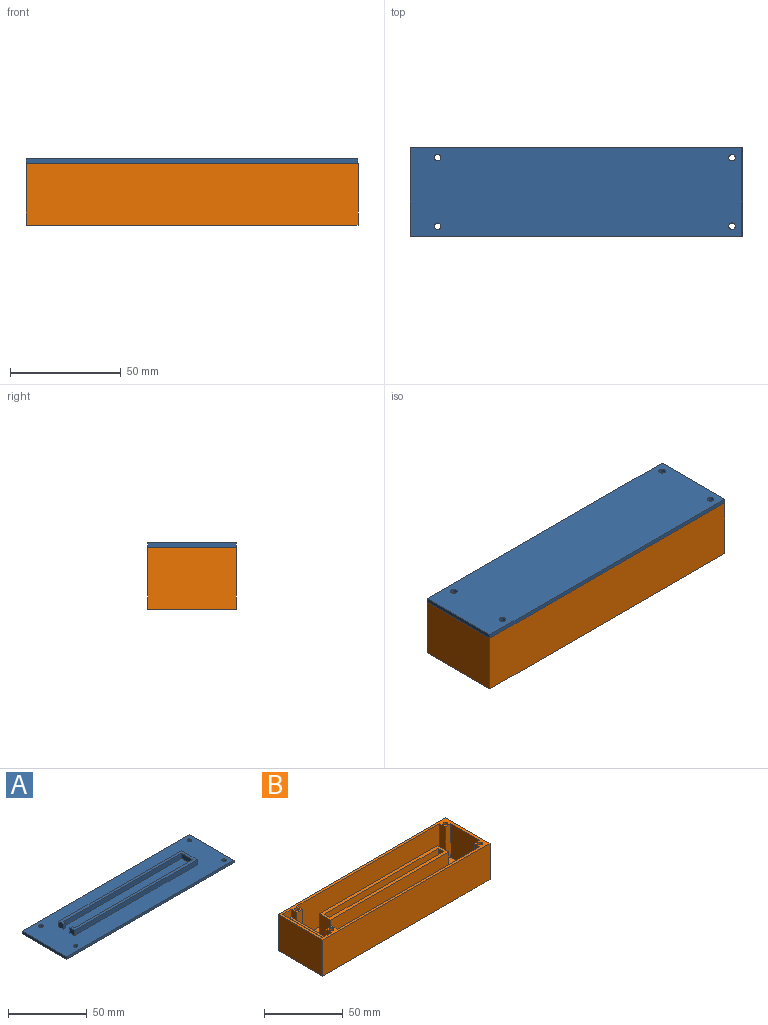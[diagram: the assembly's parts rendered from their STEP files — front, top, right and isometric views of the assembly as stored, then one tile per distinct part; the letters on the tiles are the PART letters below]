
ASSEMBLY  parts=2 mates=1
PART A: 23 faces, bbox 150x40x6 mm
  f0: plane 150x2mm, normal (0,-1,0), area 300mm2, adj f1,f6,f8,f9
  f1: plane 40x2mm, normal (1,0,0), area 80mm2, adj f0,f2,f8,f9
  f2: plane 150x2mm, normal (0,1,0), area 300mm2, adj f1,f6,f8,f9
  f3: cylinder r=1.5mm len=3mm, axis (0,0,-1), area 18.8mm2, adj f8,f9
  f4: cylinder r=1.5mm len=3mm, axis (0,0,-1), area 18.8mm2, adj f8,f9
  f5: cylinder r=1.5mm len=3mm, axis (0,0,-1), area 18.8mm2, adj f8,f9
  f6: plane 40x2mm, normal (-1,0,0), area 80mm2, adj f0,f2,f8,f9
  f7: cylinder r=1.5mm len=3mm, axis (0,0,-1), area 18.8mm2, adj f8,f9
  f8: plane 150x40mm, normal (0,0,1), area 5503.7mm2, adj f0,f1,f2,f3,f4,f5,f6,f7
  f9: plane 150x40mm, normal (0,0,-1), area 5971.7mm2, adj f0,f1,f2,f3,f4,f5,f6,f7
  f10: plane 4x2mm, normal (1,0,0), area 8mm2, adj f8,f11,f21,f22
  f11: plane 4x2mm, normal (0,1,0), area 8mm2, adj f8,f10,f12,f22
  f12: plane 4x4mm, normal (-1,0,0), area 16mm2, adj f8,f11,f13,f22
  f13: plane 110x4mm, normal (0,-1,0), area 440mm2, adj f8,f12,f14,f22
  f14: plane 14x4mm, normal (1,0,0), area 56mm2, adj f8,f13,f15,f22
  f15: plane 110x4mm, normal (0,1,0), area 440mm2, adj f8,f14,f16,f22
  f16: plane 4x4mm, normal (-1,0,0), area 16mm2, adj f8,f15,f17,f22
  f17: plane 4x2mm, normal (0,-1,0), area 8mm2, adj f8,f16,f18,f22
  f18: plane 4x2mm, normal (1,0,0), area 8mm2, adj f8,f17,f19,f22
  f19: plane 106x4mm, normal (0,-1,0), area 424mm2, adj f8,f18,f20,f22
  f20: plane 10x4mm, normal (-1,0,0), area 40mm2, adj f8,f19,f21,f22
  f21: plane 106x4mm, normal (0,1,0), area 424mm2, adj f8,f10,f20,f22
  f22: plane 110x14mm, normal (0,0,1), area 468mm2, adj f10,f11,f12,f13,f14,f15,f16,f17
PART B: 43 faces, bbox 150x40x28 mm
  f0: plane 8x6mm, normal (0,-1,0), area 48mm2, adj f3,f13,f39,f42
  f1: plane 150x28mm, normal (0,1,0), area 4140mm2, adj f5,f6,f12,f13,f28,f39,f41,f42
  f2: plane 8x8mm, normal (0,-1,0), area 60mm2, adj f13,f14,f28,f39,f40,f41
  f3: plane 36x6mm, normal (0,0,1), area 216mm2, adj f0,f13,f27,f39
  f4: plane 150x28mm, normal (0,-1,0), area 4200mm2, adj f5,f6,f12,f28
  f5: plane 40x28mm, normal (1,0,0), area 1120mm2, adj f1,f4,f12,f28
  f6: plane 40x28mm, normal (-1,0,0), area 1120mm2, adj f1,f4,f12,f28
  f7: cylinder r=1.5mm len=28mm, axis (0,0,-1), area 263.9mm2, adj f12,f28
  f8: cylinder r=1.5mm len=28mm, axis (0,0,-1), area 263.9mm2, adj f12,f28
  f9: cylinder r=1.5mm len=28mm, axis (0,0,-1), area 263.9mm2, adj f12,f28
  f10: cylinder r=1.5mm len=28mm, axis (0,0,-1), area 263.9mm2, adj f12,f28
  f11: plane 138x36mm, normal (0,0,1), area 3808mm2, adj f15,f16,f17,f18,f19,f20,f21,f22
  f12: plane 150x40mm, normal (0,0,-1), area 5461.7mm2, adj f1,f4,f5,f6,f7,f8,f9,f10
  f13: plane 38x26mm, normal (1,0,0), area 956mm2, adj f0,f1,f2,f3,f27,f28,f41,f42
  f14: plane 6x5mm, normal (-1,0,0), area 30mm2, adj f2,f15,f28,f40
  f15: plane 26x5mm, normal (0,-1,0), area 130mm2, adj f11,f14,f16,f28,f38
  f16: plane 26x5mm, normal (1,0,0), area 130mm2, adj f11,f15,f17,f28
  f17: plane 128x26mm, normal (0,-1,0), area 3328mm2, adj f11,f16,f18,f28
  f18: plane 26x5mm, normal (-1,0,0), area 130mm2, adj f11,f17,f19,f28
  f19: plane 26x5mm, normal (0,-1,0), area 130mm2, adj f11,f18,f20,f28
  f20: plane 26x26mm, normal (-1,0,0), area 676mm2, adj f11,f19,f21,f28
  f21: plane 26x5mm, normal (0,1,0), area 130mm2, adj f11,f20,f22,f28
  f22: plane 26x5mm, normal (-1,0,0), area 130mm2, adj f11,f21,f23,f28
  f23: plane 128x26mm, normal (0,1,0), area 3328mm2, adj f11,f22,f24,f28
  f24: plane 26x5mm, normal (1,0,0), area 130mm2, adj f11,f23,f25,f28
  f25: plane 26x5mm, normal (0,1,0), area 130mm2, adj f11,f24,f26,f28,f38
  f26: plane 6x5mm, normal (-1,0,0), area 30mm2, adj f25,f27,f28,f40
  f27: plane 26x8mm, normal (0,1,0), area 168mm2, adj f3,f13,f26,f28,f39,f40
  f28: plane 150x40mm, normal (0,0,1), area 815.7mm2, adj f1,f2,f4,f5,f6,f7,f8,f9
  f29: plane 102x25mm, normal (0,-1,0), area 2550mm2, adj f12,f30,f36,f37
  f30: plane 25x5mm, normal (-1,0,0), area 125mm2, adj f12,f29,f31,f37
  f31: plane 102x25mm, normal (0,1,0), area 2550mm2, adj f12,f30,f36,f37
  f32: plane 23x10mm, normal (-1,0,0), area 230mm2, adj f11,f33,f35,f37
  f33: plane 106x23mm, normal (0,-1,0), area 2438mm2, adj f11,f32,f34,f37
  f34: plane 23x10mm, normal (1,0,0), area 230mm2, adj f11,f33,f35,f37
  f35: plane 106x23mm, normal (0,1,0), area 2438mm2, adj f11,f32,f34,f37
  f36: plane 25x5mm, normal (1,0,0), area 125mm2, adj f12,f29,f31,f37
  f37: plane 106x10mm, normal (0,0,1), area 550mm2, adj f29,f30,f31,f32,f33,f34,f35,f36
  f38: plane 26x20mm, normal (1,0,0), area 520mm2, adj f11,f15,f25,f40
  f39: plane 38x20mm, normal (-1,0,0), area 740mm2, adj f0,f1,f2,f3,f27,f40,f41,f42
  f40: plane 36x2mm, normal (0,0,1), area 72mm2, adj f2,f14,f26,f27,f38,f39
  f41: plane 6x2mm, normal (0,0,-1), area 12mm2, adj f1,f2,f13,f39
  f42: plane 6x2mm, normal (0,0,1), area 12mm2, adj f0,f1,f13,f39
PLACE A rot(axis=(-1,0,0),180deg) t=(0,-41.29,41.45)mm
PLACE B t=(0,-41.29,11.45)mm
MATE fastened B.f7 <-> A.f3  axis (0,0,1) through (70.5,-25.79,39.45)mm
